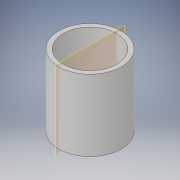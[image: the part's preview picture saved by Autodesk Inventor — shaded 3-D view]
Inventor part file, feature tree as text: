
AUTODESK INVENTOR PART (.ipt)
format: ipt  version: 2019.2 (Build 232265000, 265)  size: 106,496 bytes
history: native  units: in
note: dims shown in document units (in); Inventor stores cm internally (conversion verified against a paired STEP export)
features: sketch x2, extrude x1, revolve x1
ambient origin geometry x8: Origin, YZ Plane, XZ Plane, XY Plane, X Axis, Y Axis, Z Axis, Center Point
bodies: Solid1 (feature_tree)
feature tree (4):
  extrude  "Extrusion1"  Depth=1.75in
  revolve  "Revolution2"  [1 undecoded]
  sketch  "Sketch1"  dims[d0=1.5in d1=1.75in]
  sketch  "Sketch5"  dims[d2=2.0in d3=0.0in d6=0.0687in]
note: 1 required parameter value undecoded (feature->parameter linkage not recoverable at this tier; creation-order binding heuristic only, values carry confidence <= 0.55)
